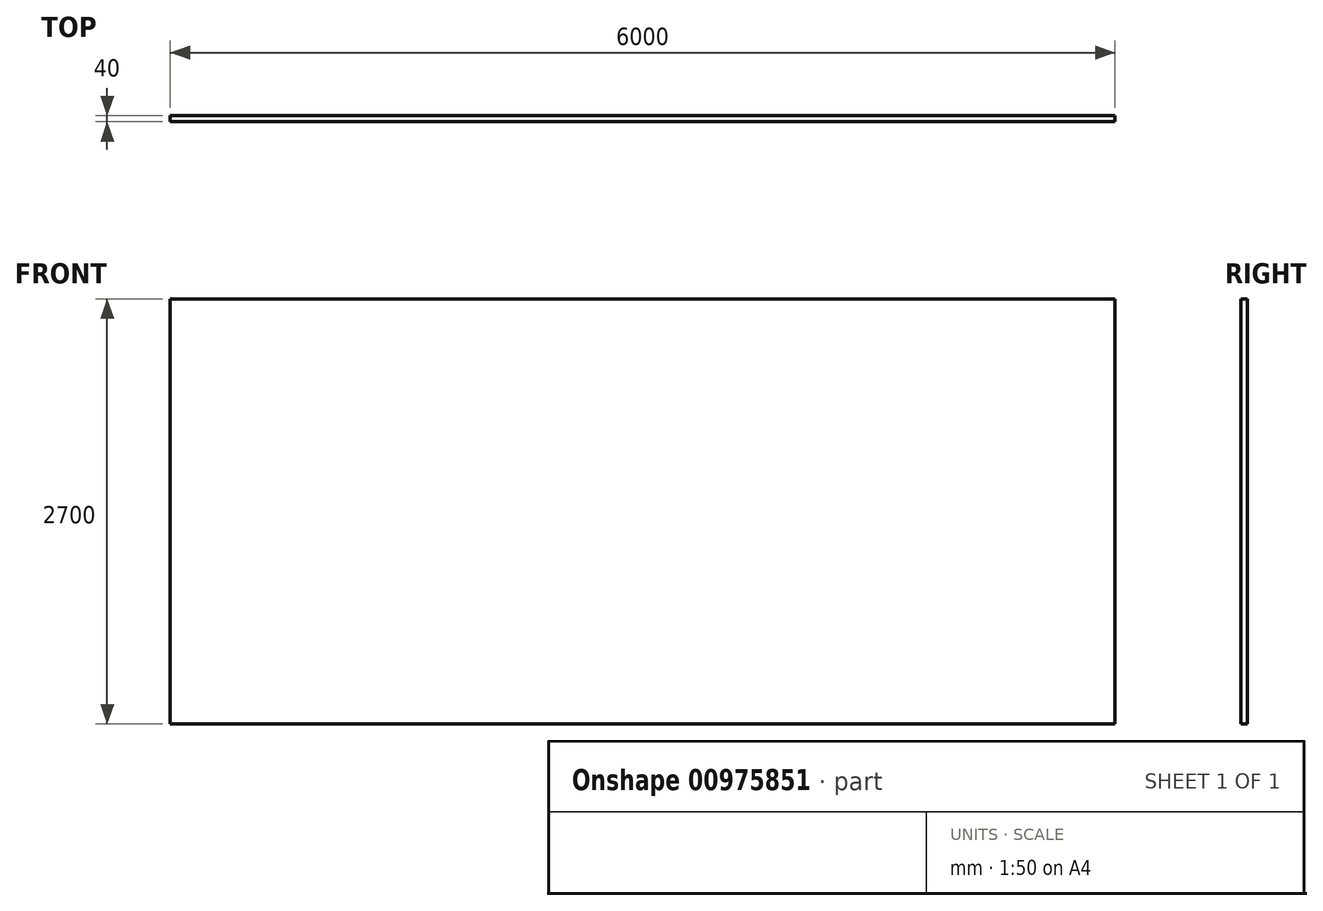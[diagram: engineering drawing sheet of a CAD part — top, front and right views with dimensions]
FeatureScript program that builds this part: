
annotation { "Feature Type Name" : "Feature", "Feature Type Description" : "" }
export const myFeature = defineFeature(function(context is Context, id is Id, definition is map)
    precondition{}
    {
        {
            var Q0;
            Q0=qCreatedBy(makeId("Front.planeOp"),FACE);
            var sketch = newSketch(context, id + "F0", { "sketchPlane" : qUnion([Q0])});
            skLineSegment(sketch, "E0.bottom", {"start": v(-2997.3, 1276.47) * mm, "end": v(3002.7, 1276.47) * mm});
            skLineSegment(sketch, "E0.top", {"start": v(-2997.3, -1423.53) * mm, "end": v(3002.7, -1423.53) * mm});
            skLineSegment(sketch, "E0.left", {"start": v(-2997.3, 1276.47) * mm, "end": v(-2997.3, -1423.53) * mm});
            skLineSegment(sketch, "E0.right", {"start": v(3002.7, 1276.47) * mm, "end": v(3002.7, -1423.53) * mm});
            skSolve(sketch);
        }
        {
            var Q0;
            Q0=makeQuery(id+"F0.imprint","IMPRINT",FACE,{"disambiguationData":[TD([[makeQuery(id+"F0.imprint","IMPRINT",EDGE,{"derivedFrom":sQuery(id+"F0.wireOp",EDGE,"E0.bottom")}),-1.0]])]});
            extrude(context, id + "F1", {"entities" : qUnion([Q0]), "depth" : 40 * mm, "offsetDistance" : 25 * mm});
        }
    });
